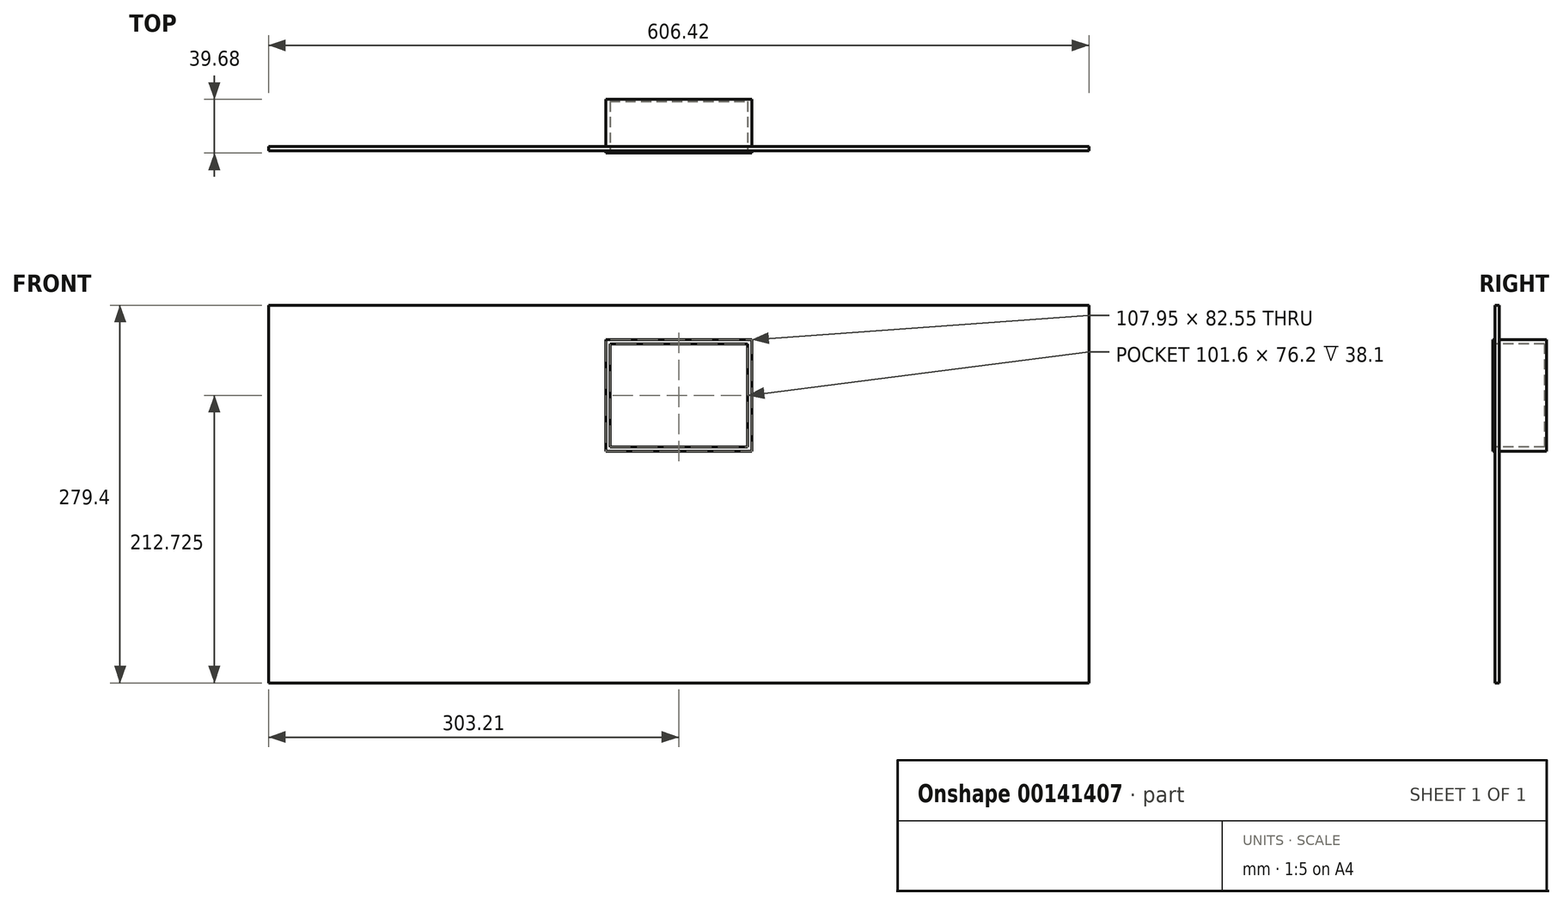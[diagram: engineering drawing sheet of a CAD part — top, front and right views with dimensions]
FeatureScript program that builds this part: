
annotation { "Feature Type Name" : "Feature", "Feature Type Description" : "" }
export const myFeature = defineFeature(function(context is Context, id is Id, definition is map)
    precondition{}
    {
        {
            var Q0;
            Q0=qCreatedBy(makeId("Front.planeOp"),FACE);
            var sketch = newSketch(context, id + "F0", { "sketchPlane" : qUnion([Q0])});
            skLineSegment(sketch, "E0.bottom", {"start": v(-303.21, 139.7) * mm, "end": v(303.21, 139.7) * mm});
            skLineSegment(sketch, "E0.top", {"start": v(-303.21, -139.7) * mm, "end": v(303.21, -139.7) * mm});
            skLineSegment(sketch, "E0.left", {"start": v(-303.21, 139.7) * mm, "end": v(-303.21, -139.7) * mm});
            skLineSegment(sketch, "E0.right", {"start": v(303.21, 139.7) * mm, "end": v(303.21, -139.7) * mm});
            skPoint(sketch, "E0.middle", {"position": v(0, 0) * mm});
            skSolve(sketch);
        }
        {
            var Q0;
            Q0=makeQuery(id+"F0.imprint","IMPRINT",FACE,{"disambiguationData":[TD([[makeQuery(id+"F0.imprint","IMPRINT",EDGE,{"derivedFrom":sQuery(id+"F0.wireOp",EDGE,"E0.bottom")}),-1.0]])]});
            extrude(context, id + "F1", {"entities" : qUnion([Q0]), "depth" : 3.17 * mm});
        }
        {
            var Q0;
            Q0=makeQuery(id+"F1.opExtrude","CAP_FACE",FACE,{"disambiguationData":[OSD([sQuery(id+"F0.wireOp",EDGE,"E0.bottom"),sQuery(id+"F0.wireOp",EDGE,"E0.top"),sQuery(id+"F0.wireOp",EDGE,"E0.left"),sQuery(id+"F0.wireOp",EDGE,"E0.right")])],"isStart":false});
            var sketch = newSketch(context, id + "F2", { "sketchPlane" : qUnion([Q0])});
            skLineSegment(sketch, "E1.bottom", {"start": v(-53.98, 114.3) * mm, "end": v(53.97, 114.3) * mm});
            skLineSegment(sketch, "E1.top", {"start": v(-53.98, 31.75) * mm, "end": v(53.97, 31.75) * mm});
            skLineSegment(sketch, "E1.left", {"start": v(-53.98, 114.3) * mm, "end": v(-53.98, 31.75) * mm});
            skLineSegment(sketch, "E1.right", {"start": v(53.98, 114.3) * mm, "end": v(53.98, 31.75) * mm});
            skPoint(sketch, "E1.middle", {"position": v(0, 73.03) * mm});
            skSolve(sketch);
        }
        {
            var Q0;
            Q0 = qSketchRegion(id + "F2", true);
            extrude(context, id + "F3", {"entities" : qUnion([Q0]), "operationType" : NewBodyOperationType.ADD, "oppositeDirection" : true, "depth" : 38.1 * mm});
        }
        {
            var Q0;
            Q0 = qSketchRegion(id + "F2", true);
            extrude(context, id + "F4", {"entities" : qUnion([Q0]), "operationType" : NewBodyOperationType.ADD, "depth" : 1.59 * mm});
        }
        {
            var Q0;
            Q0=makeQuery(id+"F4.opExtrude","CAP_FACE",FACE,{"disambiguationData":[OSD([sQuery(id+"F2.wireOp",EDGE,"E1.bottom"),sQuery(id+"F2.wireOp",EDGE,"E1.top"),sQuery(id+"F2.wireOp",EDGE,"E1.left"),sQuery(id+"F2.wireOp",EDGE,"E1.right")])],"isStart":false});
            var sketch = newSketch(context, id + "F5", { "sketchPlane" : qUnion([Q0])});
            skLineSegment(sketch, "E2.bottom", {"start": v(-50.8, 111.13) * mm, "end": v(50.8, 111.13) * mm});
            skLineSegment(sketch, "E2.top", {"start": v(-50.8, 34.92) * mm, "end": v(50.8, 34.92) * mm});
            skLineSegment(sketch, "E2.left", {"start": v(-50.8, 111.13) * mm, "end": v(-50.8, 34.92) * mm});
            skLineSegment(sketch, "E2.right", {"start": v(50.8, 111.13) * mm, "end": v(50.8, 34.92) * mm});
            skPoint(sketch, "E2.middle", {"position": v(0, 73.03) * mm});
            skSolve(sketch);
        }
        {
            var Q0;
            Q0=makeQuery(id+"F5.imprint","IMPRINT",FACE,{"disambiguationData":[TD([[makeQuery(id+"F5.imprint","IMPRINT",EDGE,{"derivedFrom":sQuery(id+"F5.wireOp",EDGE,"E2.bottom")}),-1.0]])]});
            extrude(context, id + "F6", {"entities" : qUnion([Q0]), "operationType" : NewBodyOperationType.REMOVE, "oppositeDirection" : true, "depth" : 38.1 * mm});
        }
    });
